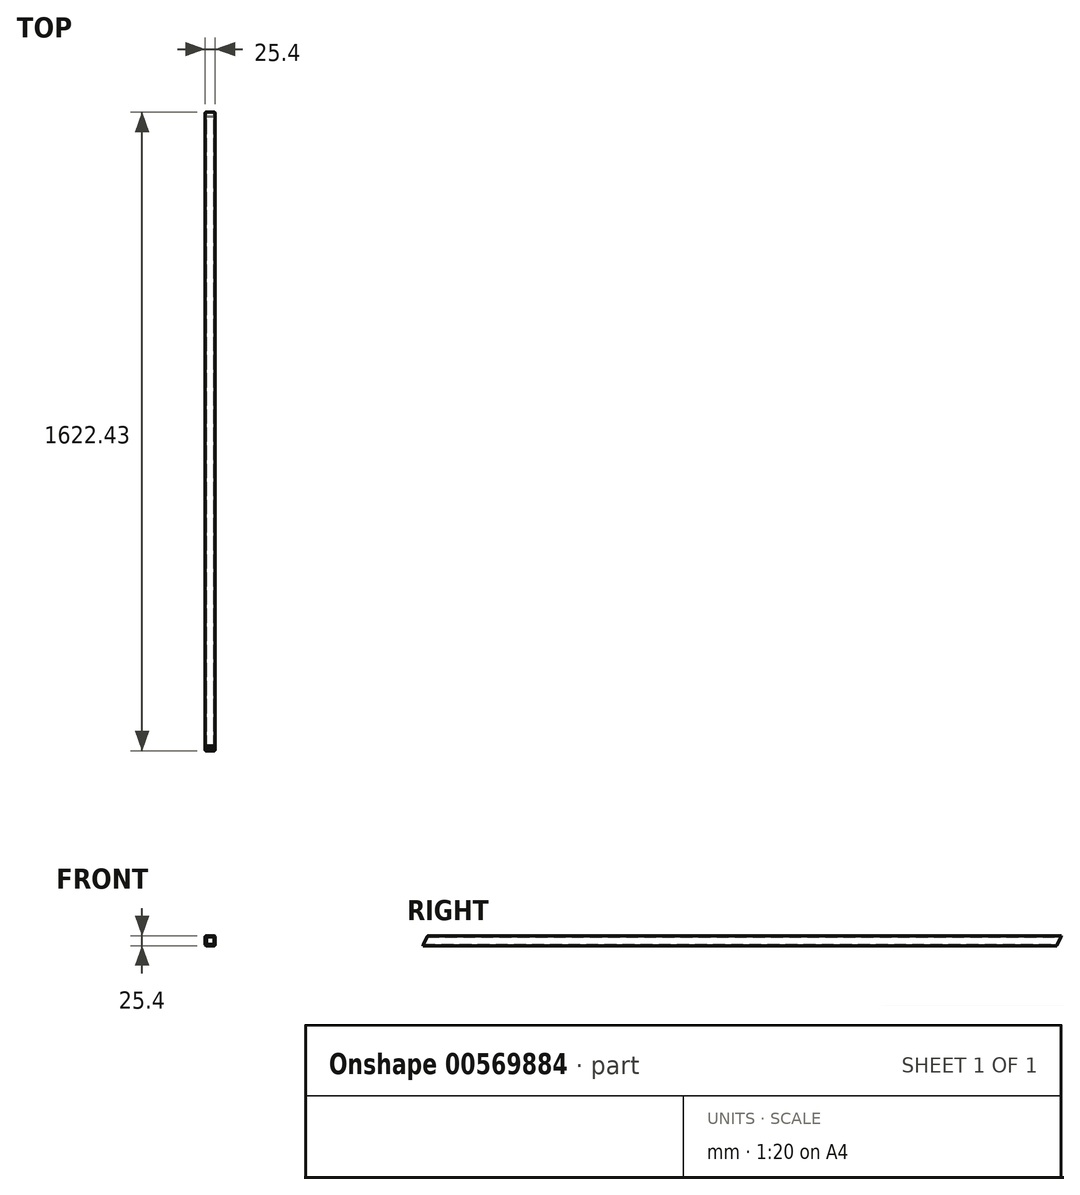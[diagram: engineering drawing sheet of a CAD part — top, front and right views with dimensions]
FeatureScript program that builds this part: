
annotation { "Feature Type Name" : "Feature", "Feature Type Description" : "" }
export const myFeature = defineFeature(function(context is Context, id is Id, definition is map)
    precondition{}
    {
        {
            var Q0;
            Q0=qCreatedBy(makeId("Front.planeOp"),FACE);
            var sketch = newSketch(context, id + "F0", { "sketchPlane" : qUnion([Q0])});
            skLineSegment(sketch, "E0.bottom", {"start": v(8.82, -12.02) * mm, "end": v(-10.23, -12.02) * mm});
            skLineSegment(sketch, "E0.top", {"start": v(8.82, 13.38) * mm, "end": v(-10.23, 13.38) * mm});
            skLineSegment(sketch, "E0.left", {"start": v(12, -8.85) * mm, "end": v(12, 10.2) * mm});
            skLineSegment(sketch, "E0.right", {"start": v(-13.4, -8.85) * mm, "end": v(-13.4, 10.2) * mm});
            skLineSegment(sketch, "E1.bottom", {"start": v(5.65, -8.85) * mm, "end": v(-7.05, -8.85) * mm});
            skLineSegment(sketch, "E1.top", {"start": v(5.65, 10.2) * mm, "end": v(-7.05, 10.2) * mm});
            skLineSegment(sketch, "E1.left", {"start": v(8.82, -5.67) * mm, "end": v(8.82, 7.03) * mm});
            skLineSegment(sketch, "E1.right", {"start": v(-10.23, -5.67) * mm, "end": v(-10.23, 7.03) * mm});
            skPoint(sketch, "E2.visualSharp", {"position": v(8.82, 10.2) * mm});
            skArc(sketch, "E2.filletArc", {"start": v(8.82, 7.03) * mm, "mid": v(7.9, 9.27) * mm, "end": v(5.65, 10.2) * mm});
            skPoint(sketch, "E3.visualSharp", {"position": v(-10.23, 10.2) * mm});
            skArc(sketch, "E3.filletArc", {"start": v(-7.05, 10.2) * mm, "mid": v(-9.3, 9.27) * mm, "end": v(-10.23, 7.03) * mm});
            skPoint(sketch, "E4.visualSharp", {"position": v(-10.23, -8.85) * mm});
            skArc(sketch, "E4.filletArc", {"start": v(-10.23, -5.67) * mm, "mid": v(-9.3, -7.92) * mm, "end": v(-7.05, -8.85) * mm});
            skPoint(sketch, "E5.visualSharp", {"position": v(8.82, -8.85) * mm});
            skArc(sketch, "E5.filletArc", {"start": v(5.65, -8.85) * mm, "mid": v(7.9, -7.92) * mm, "end": v(8.82, -5.67) * mm});
            skPoint(sketch, "E6.visualSharp", {"position": v(12, 13.38) * mm});
            skArc(sketch, "E6.filletArc", {"start": v(12, 10.2) * mm, "mid": v(11.07, 12.45) * mm, "end": v(8.82, 13.38) * mm});
            skPoint(sketch, "E7.visualSharp", {"position": v(-13.4, 13.38) * mm});
            skArc(sketch, "E7.filletArc", {"start": v(-10.23, 13.38) * mm, "mid": v(-12.47, 12.45) * mm, "end": v(-13.4, 10.2) * mm});
            skPoint(sketch, "E8.visualSharp", {"position": v(-13.4, -12.02) * mm});
            skArc(sketch, "E8.filletArc", {"start": v(-13.4, -8.85) * mm, "mid": v(-12.47, -11.1) * mm, "end": v(-10.23, -12.02) * mm});
            skPoint(sketch, "E9.visualSharp", {"position": v(12, -12.02) * mm});
            skArc(sketch, "E9.filletArc", {"start": v(8.82, -12.02) * mm, "mid": v(11.07, -11.1) * mm, "end": v(12, -8.85) * mm});
            skSolve(sketch);
        }
        {
            var Q0;
            Q0 = qSketchRegion(id + "F0", true);
            extrude(context, id + "F1", {"entities" : qUnion([Q0]), "depth" : 1622.42 * mm, "offsetDistance" : 25.4 * mm});
        }
        {
            var Q0;
            Q0=qCreatedBy(makeId("Right.planeOp"),FACE);
            var sketch = newSketch(context, id + "F2", { "sketchPlane" : qUnion([Q0])});
            skLineSegment(sketch, "E10", {"start": v(0, 13.38) * mm, "end": v(0, -13.51) * mm});
            skLineSegment(sketch, "E11", {"start": v(-12.97, -13.51) * mm, "end": v(0, 13.38) * mm});
            skLineSegment(sketch, "E12", {"start": v(0, -13.51) * mm, "end": v(-12.97, -13.51) * mm});
            skSolve(sketch);
        }
        {
            var Q0;
            Q0 = qSketchRegion(id + "F2", true);
            extrude(context, id + "F3", {"entities" : qUnion([Q0]), "operationType" : NewBodyOperationType.REMOVE, "depth" : 76.2 * mm, "offsetDistance" : 25.4 * mm, "symmetric" : true});
        }
        {
            var Q0;
            Q0=qCreatedBy(makeId("Right.planeOp"),FACE);
            var sketch = newSketch(context, id + "F4", { "sketchPlane" : qUnion([Q0])});
            skLineSegment(sketch, "E13", {"start": v(-1622.43, -12.02) * mm, "end": v(-1609.46, 14.86) * mm});
            skLineSegment(sketch, "E14", {"start": v(-1622.43, -12.02) * mm, "end": v(-1622.43, 14.86) * mm});
            skLineSegment(sketch, "E15", {"start": v(-1622.43, 14.86) * mm, "end": v(-1609.46, 14.86) * mm});
            skSolve(sketch);
        }
        {
            var Q0;
            Q0 = qSketchRegion(id + "F4", true);
            extrude(context, id + "F5", {"entities" : qUnion([Q0]), "operationType" : NewBodyOperationType.REMOVE, "depth" : 50.8 * mm, "offsetDistance" : 25.4 * mm, "symmetric" : true});
        }
    });
